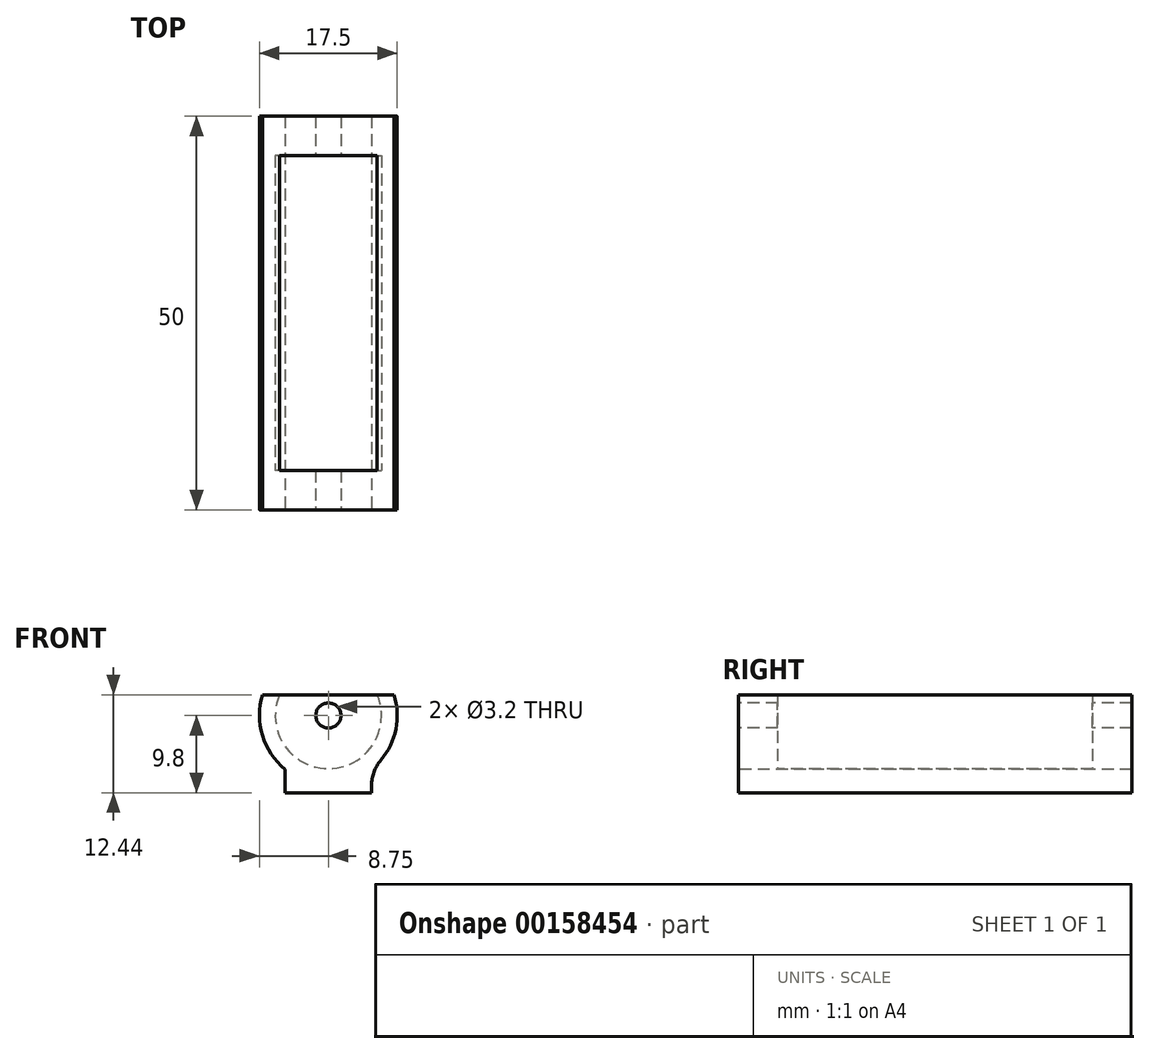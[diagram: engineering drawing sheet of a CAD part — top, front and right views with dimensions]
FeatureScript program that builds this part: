
annotation { "Feature Type Name" : "Feature", "Feature Type Description" : "" }
export const myFeature = defineFeature(function(context is Context, id is Id, definition is map)
    precondition{}
    {
        {
            var Q0;
            Q0=qCreatedBy(makeId("Front.planeOp"),FACE);
            var sketch = newSketch(context, id + "F0", { "sketchPlane" : qUnion([Q0])});
            skCircle(sketch, "E0", {"center": v(0, 0) * mm, "radius": 8.75 * mm});
            skSolve(sketch);
        }
        {
            var Q0;
            Q0 = qSketchRegion(id + "F0", true);
            extrude(context, id + "F1", {"entities" : qUnion([Q0]), "depth" : 25 * mm, "hasSecondDirection" : true, "secondDirectionOppositeDirection" : true, "secondDirectionDepth" : 25 * mm});
        }
        {
            var Q0;
            Q0=qCreatedBy(makeId("Front.planeOp"),FACE);
            var sketch = newSketch(context, id + "F2", { "sketchPlane" : qUnion([Q0])});
            skCircle(sketch, "E1", {"center": v(0, 0) * mm, "radius": 6.75 * mm});
            skSolve(sketch);
        }
        {
            var Q0;
            Q0 = qSketchRegion(id + "F2", true);
            extrude(context, id + "F3", {"entities" : qUnion([Q0]), "operationType" : NewBodyOperationType.REMOVE, "oppositeDirection" : true, "depth" : 20 * mm, "hasSecondDirection" : true, "secondDirectionOppositeDirection" : false, "secondDirectionDepth" : 20 * mm});
        }
        {
            var Q0;
            Q0=qCreatedBy(makeId("Front.planeOp"),FACE);
            var sketch = newSketch(context, id + "F4", { "sketchPlane" : qUnion([Q0])});
            skLineSegment(sketch, "E2.bottom", {"start": v(-9.2, 2.64) * mm, "end": v(9.63, 2.64) * mm});
            skLineSegment(sketch, "E2.top", {"start": v(-9.2, 9.14) * mm, "end": v(9.63, 9.14) * mm});
            skLineSegment(sketch, "E2.left", {"start": v(-9.2, 2.64) * mm, "end": v(-9.2, 9.14) * mm});
            skLineSegment(sketch, "E2.right", {"start": v(9.63, 2.64) * mm, "end": v(9.63, 9.14) * mm});
            skSolve(sketch);
        }
        {
            var Q0;
            Q0 = qSketchRegion(id + "F4", true);
            extrude(context, id + "F5", {"entities" : qUnion([Q0]), "operationType" : NewBodyOperationType.REMOVE, "endBound" : BoundingType.THROUGH_ALL, "oppositeDirection" : true, "depth" : 25 * mm, "hasSecondDirection" : true, "secondDirectionOppositeDirection" : false, "secondDirectionDepth" : 25 * mm});
        }
        {
            var Q0;
            Q0=makeQuery(id+"F1.opExtrude","CAP_FACE",FACE,{"disambiguationData":[OSD([sQuery(id+"F0.wireOp",EDGE,"E0")])],"isStart":false});
            var sketch = newSketch(context, id + "F6", { "sketchPlane" : qUnion([Q0])});
            skLineSegment(sketch, "E3.bottom", {"start": v(5.48, -6.82) * mm, "end": v(-5.48, -6.82) * mm});
            skLineSegment(sketch, "E3.top", {"start": v(5.48, -9.8) * mm, "end": v(-5.48, -9.8) * mm});
            skLineSegment(sketch, "E3.left", {"start": v(5.48, -6.82) * mm, "end": v(5.48, -9.8) * mm});
            skLineSegment(sketch, "E3.right", {"start": v(-5.48, -6.82) * mm, "end": v(-5.48, -9.8) * mm});
            skPoint(sketch, "E3.middle", {"position": v(0, -8.3) * mm});
            skSolve(sketch);
        }
        {
            var Q0;
            Q0 = qSketchRegion(id + "F6", true);
            var Q1;
            Q1=makeQuery(id+"F1.opExtrude","CAP_FACE",FACE,{"disambiguationData":[OSD([sQuery(id+"F0.wireOp",EDGE,"E0")])],"isStart":true});
            extrude(context, id + "F7", {"entities" : qUnion([Q0]), "operationType" : NewBodyOperationType.ADD, "endBound" : BoundingType.UP_TO_SURFACE, "oppositeDirection" : true, "endBoundEntityFace" : qUnion([Q1]), "depth" : 50 * mm});
        }
        {
            var Q0;
            Q0=makeQuery(id+"F7.opExtrude","SWEPT_EDGE",EDGE,{"disambiguationData":[OSD([sQuery(id+"F0.wireOp",EDGE,"E0"),sQuery(id+"F6.wireOp",EDGE,"E3.bottom"),sQuery(id+"F6.wireOp",EDGE,"E3.left")])]});
            var Q1;
            Q1=makeQuery(id+"F7.opExtrude","SWEPT_EDGE",EDGE,{"disambiguationData":[OSD([sQuery(id+"F0.wireOp",EDGE,"E0"),sQuery(id+"F6.wireOp",EDGE,"E3.bottom"),sQuery(id+"F6.wireOp",EDGE,"E3.right")])]});
            fillet(context, id + "F8", {"entities" : qUnion([Q0, Q1]), "radius" : 5 * mm, "tangentPropagation" : true, "allowEdgeOverflow" : false});
        }
        {
            var Q0;
            Q0=qCreatedBy(makeId("Front.planeOp"),FACE);
            var sketch = newSketch(context, id + "F9", { "sketchPlane" : qUnion([Q0])});
            skCircle(sketch, "E4", {"center": v(0, 0) * mm, "radius": 1.6 * mm});
            skSolve(sketch);
        }
        {
            var Q0;
            Q0=makeQuery(id+"F9.imprint","IMPRINT",FACE,{"disambiguationData":[TD([[makeQuery(id+"F9.imprint","IMPRINT",EDGE,{"derivedFrom":sQuery(id+"F9.wireOp",EDGE,"E4")}),1.0]])]});
            var Q1;
            Q1=sQuery(id+"F9.wireOp",EDGE,"E4");
            extrude(context, id + "F10", {"entities" : qUnion([Q0]), "operationType" : NewBodyOperationType.REMOVE, "surfaceEntities" : qUnion([Q1]), "endBound" : BoundingType.THROUGH_ALL, "oppositeDirection" : true, "depth" : 25 * mm, "hasSecondDirection" : true, "secondDirectionBound" : SecondDirectionBoundingType.THROUGH_ALL, "secondDirectionOppositeDirection" : false, "secondDirectionDepth" : 25 * mm});
        }
    });
